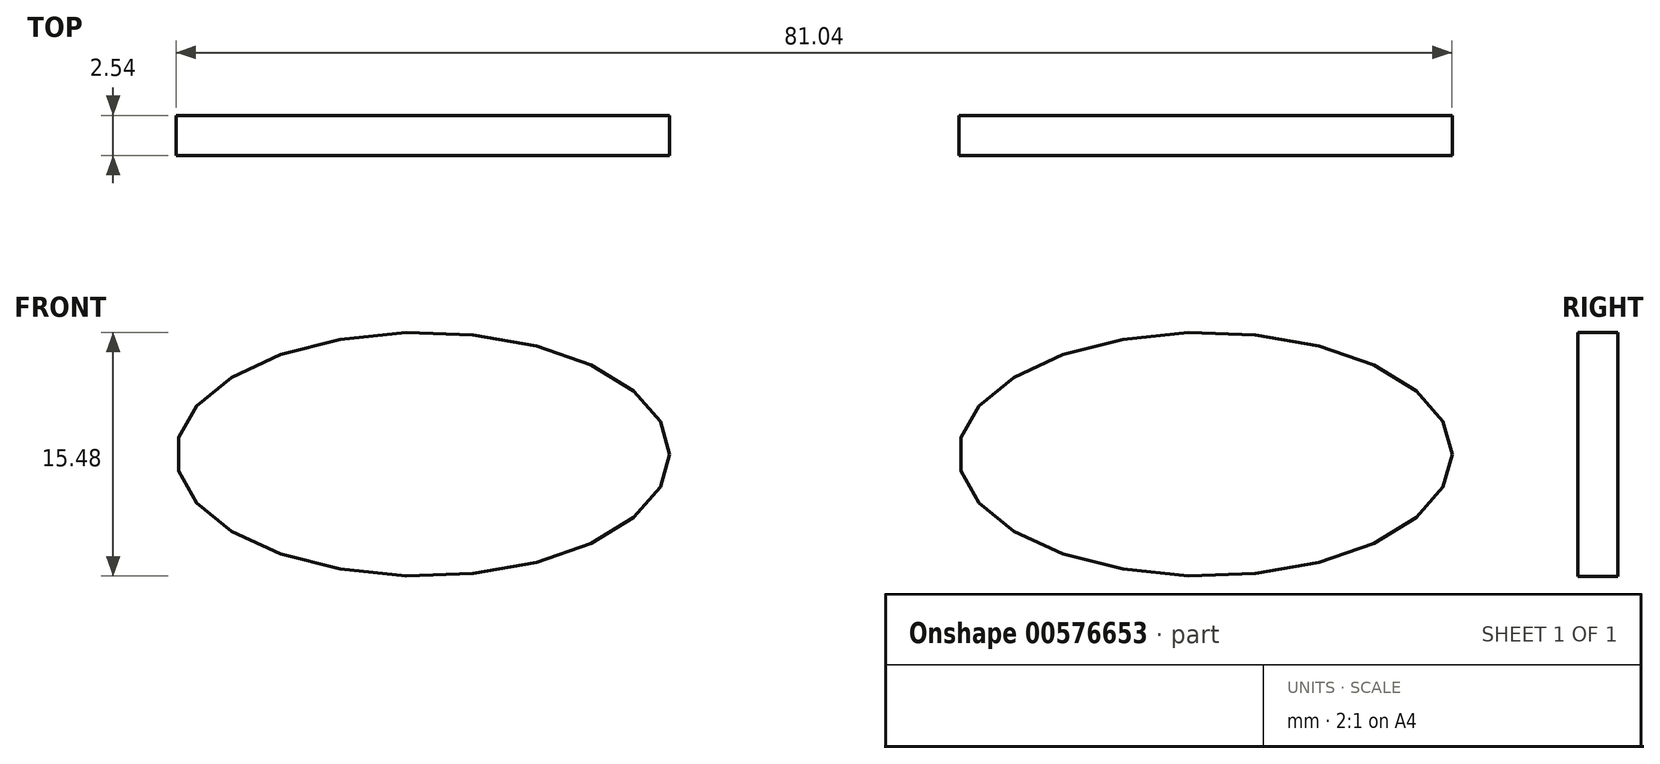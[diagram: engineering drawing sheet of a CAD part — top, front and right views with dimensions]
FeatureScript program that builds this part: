
annotation { "Feature Type Name" : "Feature", "Feature Type Description" : "" }
export const myFeature = defineFeature(function(context is Context, id is Id, definition is map)
    precondition{}
    {
        {
            var Q0;
            Q0=qCreatedBy(makeId("Front.planeOp"),FACE);
            var sketch = newSketch(context, id + "F0", { "sketchPlane" : qUnion([Q0])});
            skEllipse(sketch, "E0", {"center": v(-24.9, 0) * mm, "majorRadius": 15.67 * mm, "minorRadius": 7.74 * mm, "majorAxis": v(1, 0)});
            skSolve(sketch);
        }
        {
            var Q0;
            Q0=makeQuery(id+"F0.imprint","IMPRINT",FACE,{"disambiguationData":[TD([[makeQuery(id+"F0.imprint","IMPRINT",EDGE,{"derivedFrom":sQuery(id+"F0.wireOp",EDGE,"E0")}),1.0]])]});
            var sketch = newSketch(context, id + "F1", { "sketchPlane" : qUnion([Q0])});
            skEllipse(sketch, "E1", {"center": v(24.81, 0) * mm, "majorRadius": 15.67 * mm, "minorRadius": 7.74 * mm, "majorAxis": v(1, 0)});
            skSolve(sketch);
        }
        {
            var Q0;
            Q0=makeQuery(id+"F0.imprint","IMPRINT",FACE,{"disambiguationData":[TD([[makeQuery(id+"F0.imprint","IMPRINT",EDGE,{"derivedFrom":sQuery(id+"F0.wireOp",EDGE,"E0")}),1.0]])]});
            extrude(context, id + "F2", {"entities" : qUnion([Q0]), "depth" : 2.54 * mm, "offsetDistance" : 25.4 * mm});
        }
        {
            var Q0;
            Q0=makeQuery(id+"F1.imprint","IMPRINT",FACE,{"disambiguationData":[TD([[makeQuery(id+"F1.imprint","IMPRINT",EDGE,{"derivedFrom":sQuery(id+"F1.wireOp",EDGE,"E1")}),1.0]])]});
            extrude(context, id + "F3", {"entities" : qUnion([Q0]), "depth" : 2.54 * mm, "offsetDistance" : 25.4 * mm});
        }
    });
